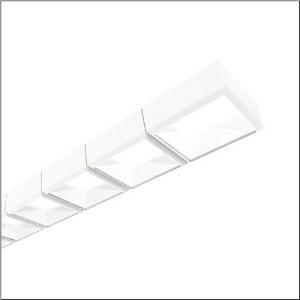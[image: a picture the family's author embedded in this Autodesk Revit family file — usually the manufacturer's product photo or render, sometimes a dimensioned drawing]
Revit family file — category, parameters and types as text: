
# Revit family: scriptus_r__11_5mz214d0twa_b782
name_source: partatom
category: Lighting Fixtures
units: mm (PartAtom-declared; Revit-internal decimal feet)

## family parameters
Cut with Voids When Loaded = No
Host = Face
Light Source = No
Part Type = Normal
Room Calculation Point = No
Round Connector Dimension = Use Diameter
Shared = No

## types (1)
- --- (1 x LED 3000K+6500K / CRI = 80 (unbekannt), 3600 lm, 3000K)
    Apparent Load = 53 VA
    CIE Flux Codes = 82 95 99 100 100
    Color Rendering = 80
    Color Temperature = 3000K
    Default Elevation = 1800 mm
    Description = Scriptus® 11, office luminaire, primary optical cover: lenses, CAT 2 (L<= 3000cd/m²), light emission: direct distribution, primary light characteristic: symmetric, installation type: surface-mounted, LED, rated luminous flux: 7.190lm, luminous efficacy: 137lm/W, light colour: 8tw, colour temperature: 3000..6500K, control gear: DALI, with terminal, 5-pole, mains connection: 230V, AC, 50Hz, rated input power: 53W, housing, luminaire housing, of aluminium, traffic white (RAL 9016), length: 3.088mm, width: 114mm, height: 57mm, protection rating (complete): IP20, insulation class (complete): insulation class I (protective earthing), certification: CE, protection symbol: F, permissible operating ambient temperature: 0..+35°C, standard: EN 50419, packaging unit: 1 piece
    Height = 57 mm
    Lamp = 1 x LED 3000K+6500K / CRI >= 80 (unbekannt)
    Lamp Light Flux = 3600 lm
    Lamp count = 1
    Length = 3088 mm
    Luminous efficacy = 137 lm/W
    Manufacturer = Siteco
    ModVariant = No
    Model = 5MZ214D0TWA
    Mounting Place = Ceiling
    Mounting Type = Surface mounted
    Number of Poles = 1
    OnlyDefault = Yes
    Power Factor = 1
    Product Name = Scriptus® 11
    Product group = office luminaire | ceiling mounted
    ProductGroupID = 302
    Protection Class = Protection class I
    Protection Degree = IP 20
    RLX_Detail_Level = 1
    RLX_Emergency_Light_Flux = 0 lm
    RLX_Emergency_Type = 0
    RLX_Emergency_Type_DB = No
    RlxData = <blob elided: 30425 chars, md5=f8326a9d>
    Socket = socket
    Standby Power = 0 W
    System Light Flux = 7200 lm
    System Power = 53 W
    Type Comments = individual setting: colour temperature 6500K
    Type Image = l_1004833.jpg
    URL = http://relux.com
    VarID = @adj_203152
    Voltage = 0 V
    Weight = 0.00 kg
    Width = 114 mm

## geometry (parser evidence)
native form markers: Blend x4, Sweep x14
no freeform markers — native parametric forms only
